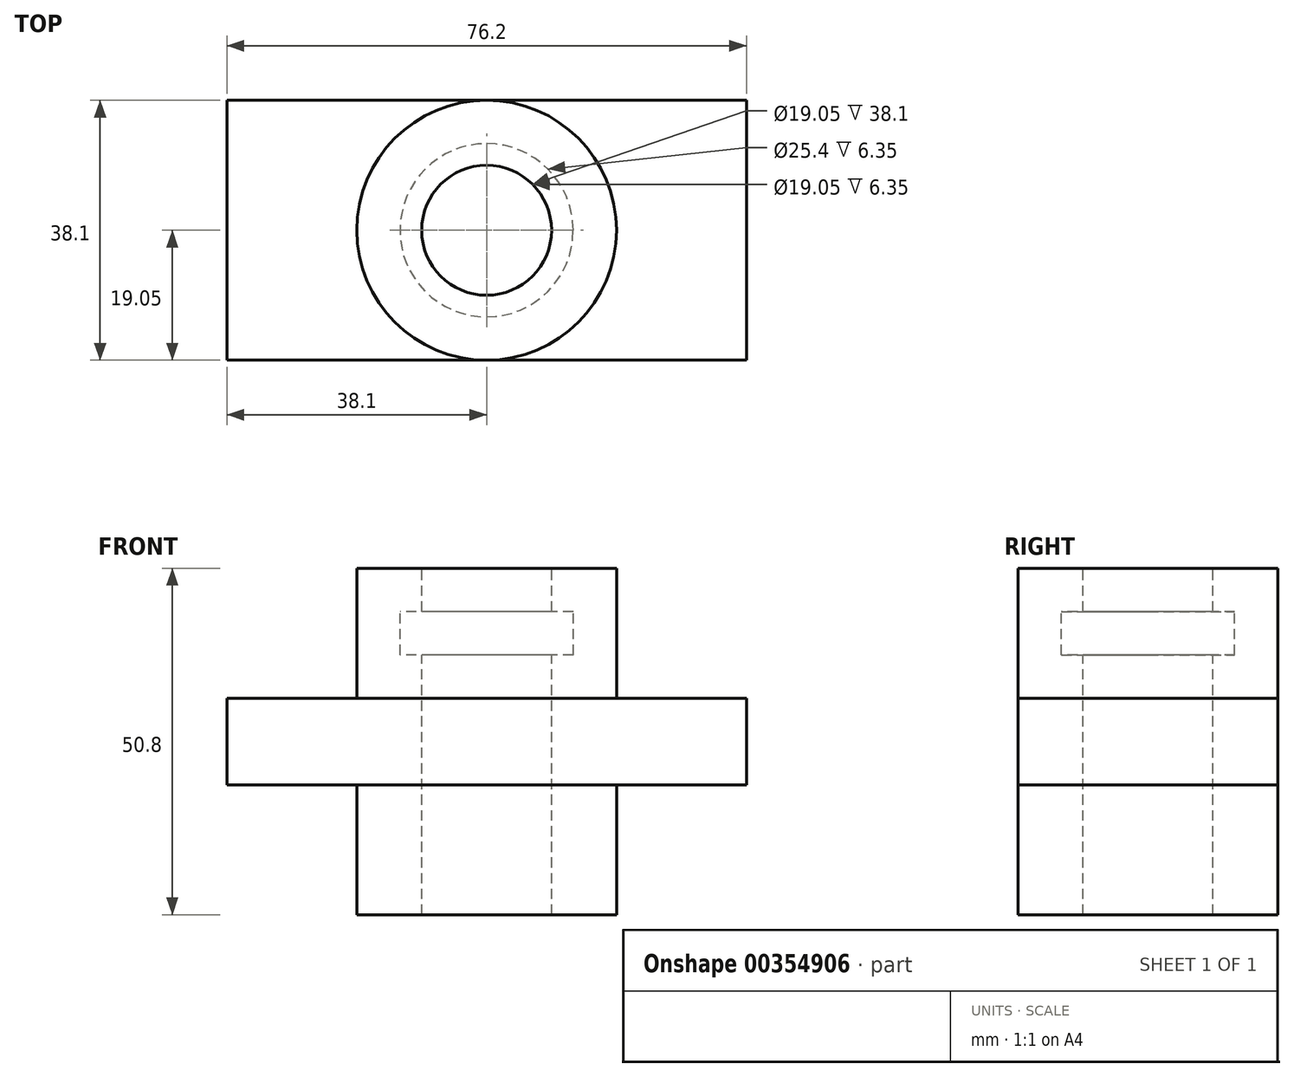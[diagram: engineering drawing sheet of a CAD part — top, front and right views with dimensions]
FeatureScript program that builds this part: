
annotation { "Feature Type Name" : "Feature", "Feature Type Description" : "" }
export const myFeature = defineFeature(function(context is Context, id is Id, definition is map)
    precondition{}
    {
        {
            var Q0;
            Q0=qCreatedBy(makeId("Front.planeOp"),FACE);
            var sketch = newSketch(context, id + "F0", { "sketchPlane" : qUnion([Q0])});
            skLineSegment(sketch, "E0", {"start": v(0, 0) * mm, "end": v(0, 12.7) * mm});
            skLineSegment(sketch, "E1", {"start": v(0, 12.7) * mm, "end": v(76.2, 12.7) * mm});
            skLineSegment(sketch, "E2", {"start": v(76.2, 12.7) * mm, "end": v(76.2, 0) * mm});
            skLineSegment(sketch, "E3", {"start": v(76.2, 0) * mm, "end": v(0, 0) * mm});
            skSolve(sketch);
        }
        {
            var Q0;
            Q0=makeQuery(id+"F0.imprint","IMPRINT",FACE,{"disambiguationData":[TD([[makeQuery(id+"F0.imprint","IMPRINT",EDGE,{"derivedFrom":sQuery(id+"F0.wireOp",EDGE,"E0")}),-1.0]])]});
            extrude(context, id + "F1", {"entities" : qUnion([Q0]), "oppositeDirection" : true, "depth" : 38.1 * mm});
        }
        {
            var Q0;
            Q0=makeQuery(id+"F1.opExtrude","SWEPT_FACE",FACE,{"disambiguationData":[OSD([sQuery(id+"F0.wireOp",EDGE,"E1")])]});
            var sketch = newSketch(context, id + "F2", { "sketchPlane" : qUnion([Q0])});
            skLineSegment(sketch, "E4", {"start": v(0, 0) * mm, "end": v(0, 19.05) * mm, "construction": true});
            skLineSegment(sketch, "E5", {"start": v(0, 19.05) * mm, "end": v(38.1, 19.05) * mm, "construction": true});
            skCircle(sketch, "E6", {"center": v(38.1, 19.05) * mm, "radius": 19.05 * mm});
            skSolve(sketch);
        }
        {
            var Q0;
            {var subQ0=sQuery(id+"F2.wireOp",EDGE,"E6");var subQ1=sQuery(id+"F0.wireOp",EDGE,"E1");var subQ2=makeQuery(id+"F2.imprint","INTERSECT",VERTEX,{"derivedFrom":[makeQuery(id+"F1.opExtrude","CAP_EDGE",EDGE,{"disambiguationData":[OSD([subQ1])],"isStart":true}),subQ0]});Q0=makeQuery(id+"F2.imprint","IMPRINT",FACE,{"disambiguationData":[TD([[makeQuery(id+"F2.imprint","IMPRINT",EDGE,{"disambiguationData":[TD([[subQ2,1.0]])],"derivedFrom":subQ0}),1.0]])]});}
            extrude(context, id + "F3", {"entities" : qUnion([Q0]), "operationType" : NewBodyOperationType.ADD, "depth" : 12.7 * mm, "hasSecondDirection" : true, "secondDirectionOppositeDirection" : true, "secondDirectionDepth" : 31.75 * mm});
        }
        {
            var Q0;
            Q0=makeQuery(id+"F3.opExtrude","CAP_FACE",FACE,{"disambiguationData":[OSD([sQuery(id+"F2.wireOp",EDGE,"E6")])],"isStart":false});
            var sketch = newSketch(context, id + "F4", { "sketchPlane" : qUnion([Q0])});
            skCircle(sketch, "E7", {"center": v(38.1, 19.05) * mm, "radius": 1.26 * mm});
            skSolve(sketch);
        }
        {
            var Q0;
            Q0=sQuery(id+"F4.wireOp",VERTEX,"E7.center");
            var Q1;
            Q1=makeQuery(id+"F1.opExtrude","SWEPT_BODY",BODY,{"disambiguationData":[OSD([sQuery(id+"F0.wireOp",EDGE,"E0"),sQuery(id+"F0.wireOp",EDGE,"E1"),sQuery(id+"F0.wireOp",EDGE,"E2"),sQuery(id+"F0.wireOp",EDGE,"E3")])]});
            hole(context, id + "F5", {"style" : HoleStyle.C_BORE, "endStyle" : HoleEndStyle.THROUGH, "holeDiameter" : 19.05 * mm, "cBoreDiameter" : 25.4 * mm, "cBoreDepth" : 6.35 * mm, "isTappedThrough" : true, "tappedDepth" : 12.7 * mm, "tapClearance" : 3, "locations" : qUnion([Q0]), "scope" : qUnion([Q1])});
        }
        {
            var Q0;
            Q0=makeQuery(id+"F3.opExtrude","CAP_FACE",FACE,{"disambiguationData":[OSD([sQuery(id+"F2.wireOp",EDGE,"E6")])],"isStart":false});
            var sketch = newSketch(context, id + "F6", { "sketchPlane" : qUnion([Q0])});
            skCircle(sketch, "E8", {"center": v(38.1, 19.05) * mm, "radius": 19.05 * mm});
            skSolve(sketch);
        }
        {
            var Q0;
            Q0 = qSketchRegion(id + "F6", true);
            extrude(context, id + "F7", {"entities" : qUnion([Q0]), "operationType" : NewBodyOperationType.ADD, "depth" : 6.35 * mm});
        }
        {
            var Q0;
            Q0=makeQuery(id+"F7.opExtrude","CAP_FACE",FACE,{"disambiguationData":[OSD([sQuery(id+"F6.wireOp",EDGE,"E8")])],"isStart":false});
            var sketch = newSketch(context, id + "F8", { "sketchPlane" : qUnion([Q0])});
            skPoint(sketch, "E9", {"position": v(38.1, 19.05) * mm});
            skCircle(sketch, "E10", {"center": v(38.1, 19.05) * mm, "radius": 9.53 * mm});
            skSolve(sketch);
        }
        {
            var Q0;
            Q0=makeQuery(id+"F8.imprint","IMPRINT",FACE,{"disambiguationData":[TD([[makeQuery(id+"F8.imprint","IMPRINT",EDGE,{"derivedFrom":sQuery(id+"F8.wireOp",EDGE,"E10")}),1.0]])]});
            extrude(context, id + "F9", {"entities" : qUnion([Q0]), "operationType" : NewBodyOperationType.REMOVE, "oppositeDirection" : true, "depth" : 6.35 * mm});
        }
    });
